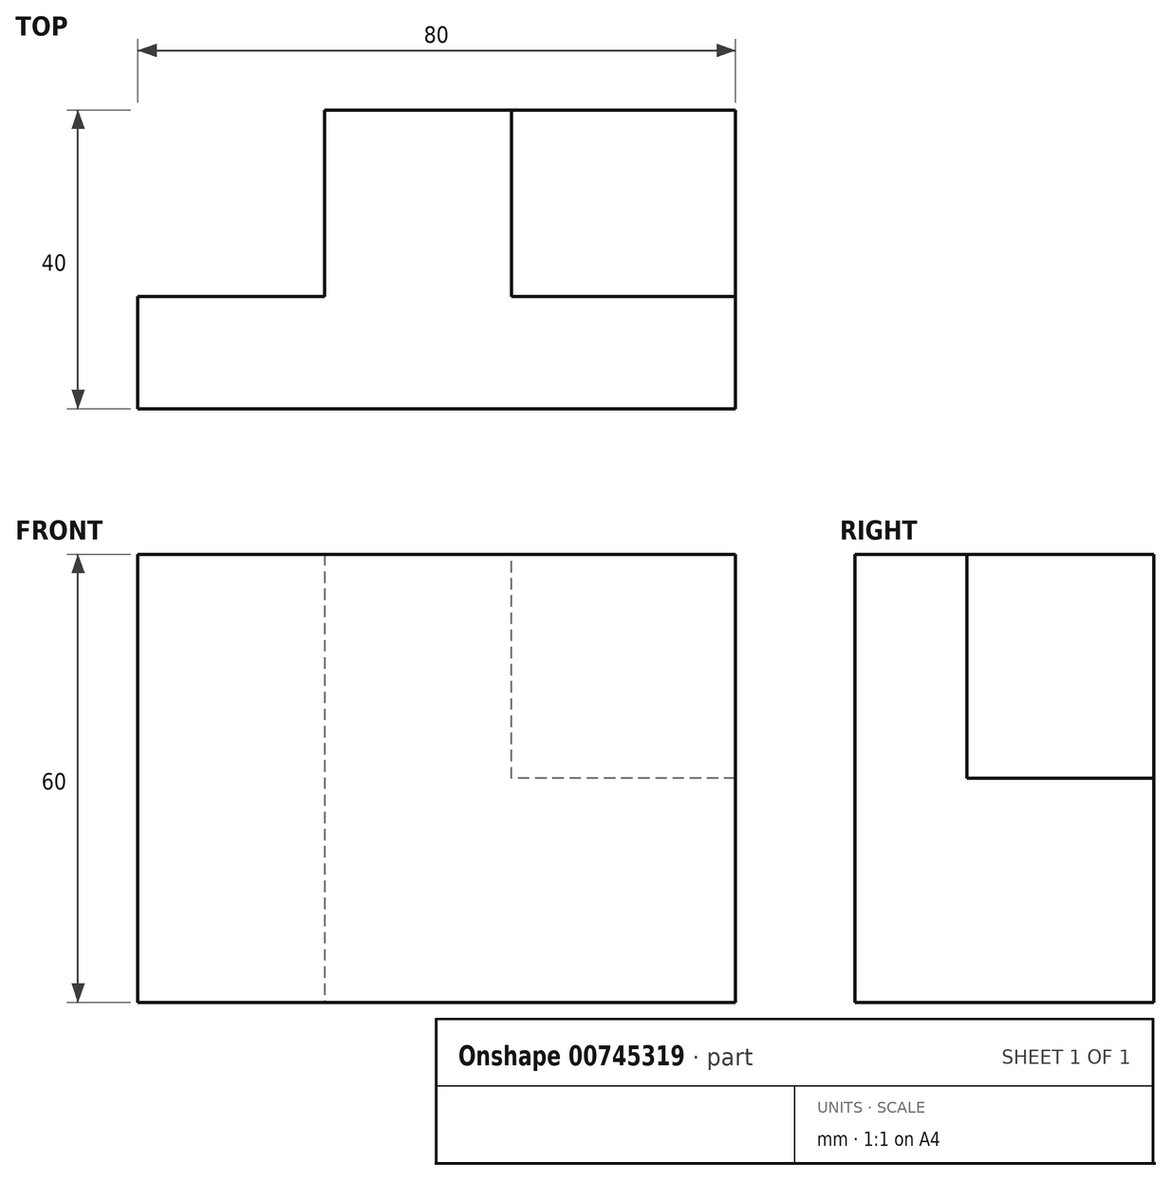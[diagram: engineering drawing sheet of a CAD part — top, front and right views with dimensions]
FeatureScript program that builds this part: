
annotation { "Feature Type Name" : "Feature", "Feature Type Description" : "" }
export const myFeature = defineFeature(function(context is Context, id is Id, definition is map)
    precondition{}
    {
        {
            var Q0;
            Q0=qCreatedBy(makeId("Front.planeOp"),FACE);
            var sketch = newSketch(context, id + "F0", { "sketchPlane" : qUnion([Q0])});
            skLineSegment(sketch, "E0", {"start": v(-80, 60) * mm, "end": v(-80, 0) * mm});
            skLineSegment(sketch, "E1", {"start": v(-80, 0) * mm, "end": v(0, 0) * mm});
            skLineSegment(sketch, "E2", {"start": v(0, 0) * mm, "end": v(0, 60) * mm});
            skLineSegment(sketch, "E3", {"start": v(0, 60) * mm, "end": v(-80, 60) * mm});
            skSolve(sketch);
        }
        {
            var Q0;
            Q0=makeQuery(id+"F0.imprint","IMPRINT",FACE,{"disambiguationData":[TD([[makeQuery(id+"F0.imprint","IMPRINT",EDGE,{"derivedFrom":sQuery(id+"F0.wireOp",EDGE,"E0")}),1.0]])]});
            extrude(context, id + "F1", {"entities" : qUnion([Q0]), "depth" : 15 * mm, "offsetDistance" : 25 * mm});
        }
        {
            var Q0;
            Q0=qCreatedBy(makeId("Front.planeOp"),FACE);
            var sketch = newSketch(context, id + "F2", { "sketchPlane" : qUnion([Q0])});
            skLineSegment(sketch, "E4", {"start": v(0, 0) * mm, "end": v(0, 30) * mm});
            skLineSegment(sketch, "E5", {"start": v(0, 30) * mm, "end": v(-30, 30) * mm});
            skLineSegment(sketch, "E6", {"start": v(-30, 30) * mm, "end": v(-30, 60) * mm});
            skLineSegment(sketch, "E7", {"start": v(-55, 53.42) * mm, "end": v(-55, 0) * mm});
            skLineSegment(sketch, "E8", {"start": v(-55, 0) * mm, "end": v(0, 0) * mm});
            skLineSegment(sketch, "E9", {"start": v(0, 30) * mm, "end": v(0, 0) * mm});
            skLineSegment(sketch, "E10", {"start": v(-30, 60) * mm, "end": v(-30, 60) * mm});
            skLineSegment(sketch, "E11", {"start": v(-30, 60) * mm, "end": v(-55, 60) * mm});
            skLineSegment(sketch, "E12", {"start": v(-55, 60) * mm, "end": v(-55, 53.42) * mm});
            skSolve(sketch);
        }
        {
            var Q0;
            Q0=makeQuery(id+"F2.imprint","IMPRINT",FACE,{"disambiguationData":[TD([[makeQuery(id+"F2.imprint","IMPRINT",EDGE,{"derivedFrom":sQuery(id+"F2.wireOp",EDGE,"E5")}),1.0]])]});
            extrude(context, id + "F3", {"entities" : qUnion([Q0]), "operationType" : NewBodyOperationType.ADD, "oppositeDirection" : true, "depth" : 25 * mm, "offsetDistance" : 25 * mm});
        }
    });
